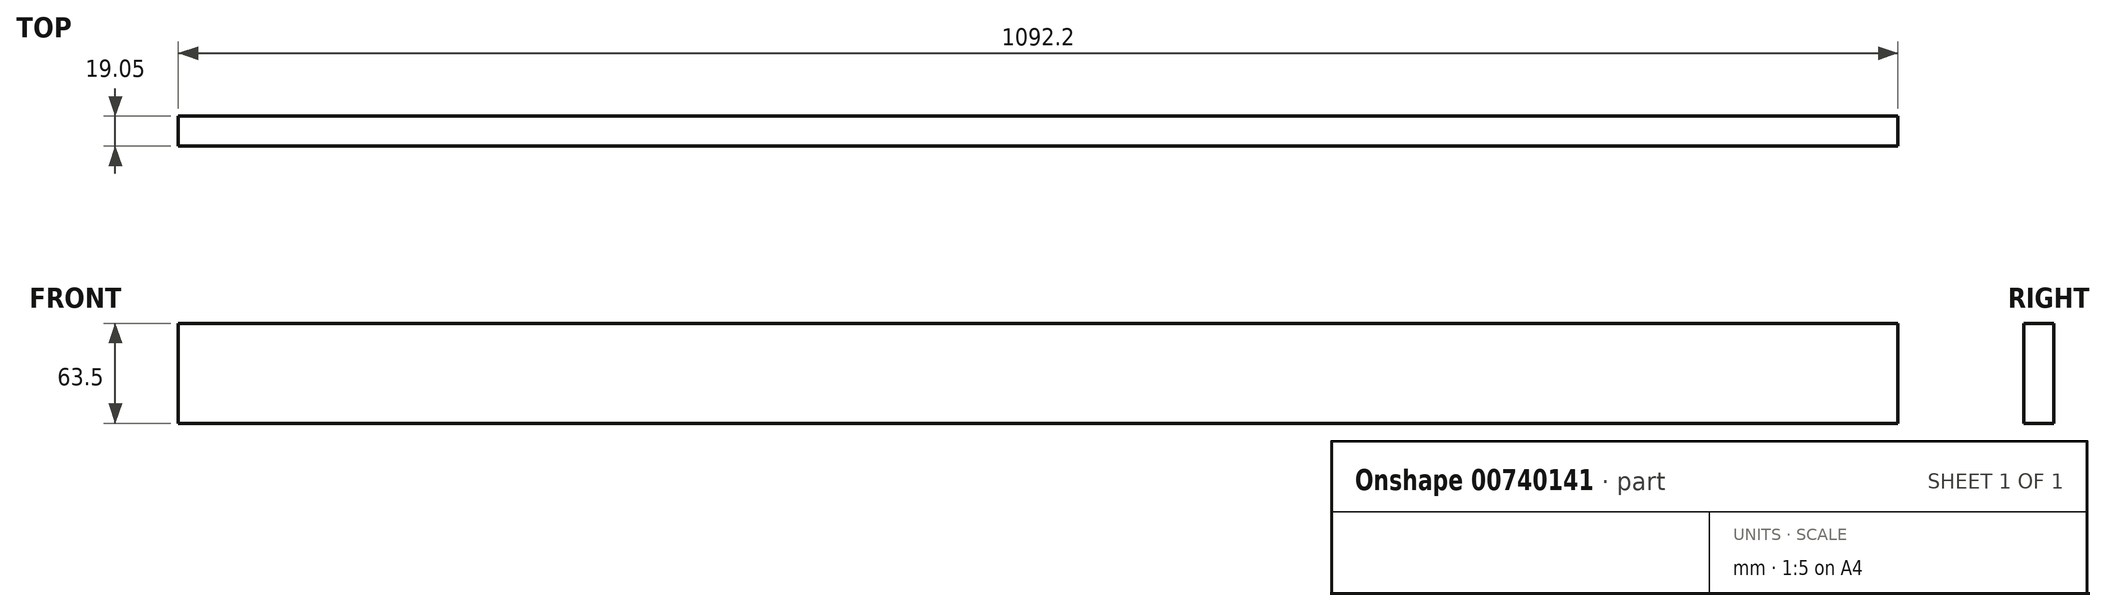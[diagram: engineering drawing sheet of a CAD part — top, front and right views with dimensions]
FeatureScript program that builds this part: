
annotation { "Feature Type Name" : "Feature", "Feature Type Description" : "" }
export const myFeature = defineFeature(function(context is Context, id is Id, definition is map)
    precondition{}
    {
        {
            var Q0;
            Q0=qCreatedBy(makeId("Right.planeOp"),FACE);
            var sketch = newSketch(context, id + "F0", { "sketchPlane" : qUnion([Q0])});
            skLineSegment(sketch, "E0.bottom", {"start": v(-79.68, 59.96) * mm, "end": v(-60.63, 59.96) * mm});
            skLineSegment(sketch, "E0.top", {"start": v(-79.68, -3.54) * mm, "end": v(-60.63, -3.54) * mm});
            skLineSegment(sketch, "E0.left", {"start": v(-79.68, 59.96) * mm, "end": v(-79.68, -3.54) * mm});
            skLineSegment(sketch, "E0.right", {"start": v(-60.63, 59.96) * mm, "end": v(-60.63, -3.54) * mm});
            skSolve(sketch);
        }
        {
            var Q0;
            Q0=makeQuery(id+"F0.imprint","IMPRINT",FACE,{"disambiguationData":[TD([[makeQuery(id+"F0.imprint","IMPRINT",EDGE,{"derivedFrom":sQuery(id+"F0.wireOp",EDGE,"E0.bottom")}),-1.0]])]});
            extrude(context, id + "F1", {"entities" : qUnion([Q0]), "depth" : 1092.2 * mm, "offsetDistance" : 25.4 * mm});
        }
    });
